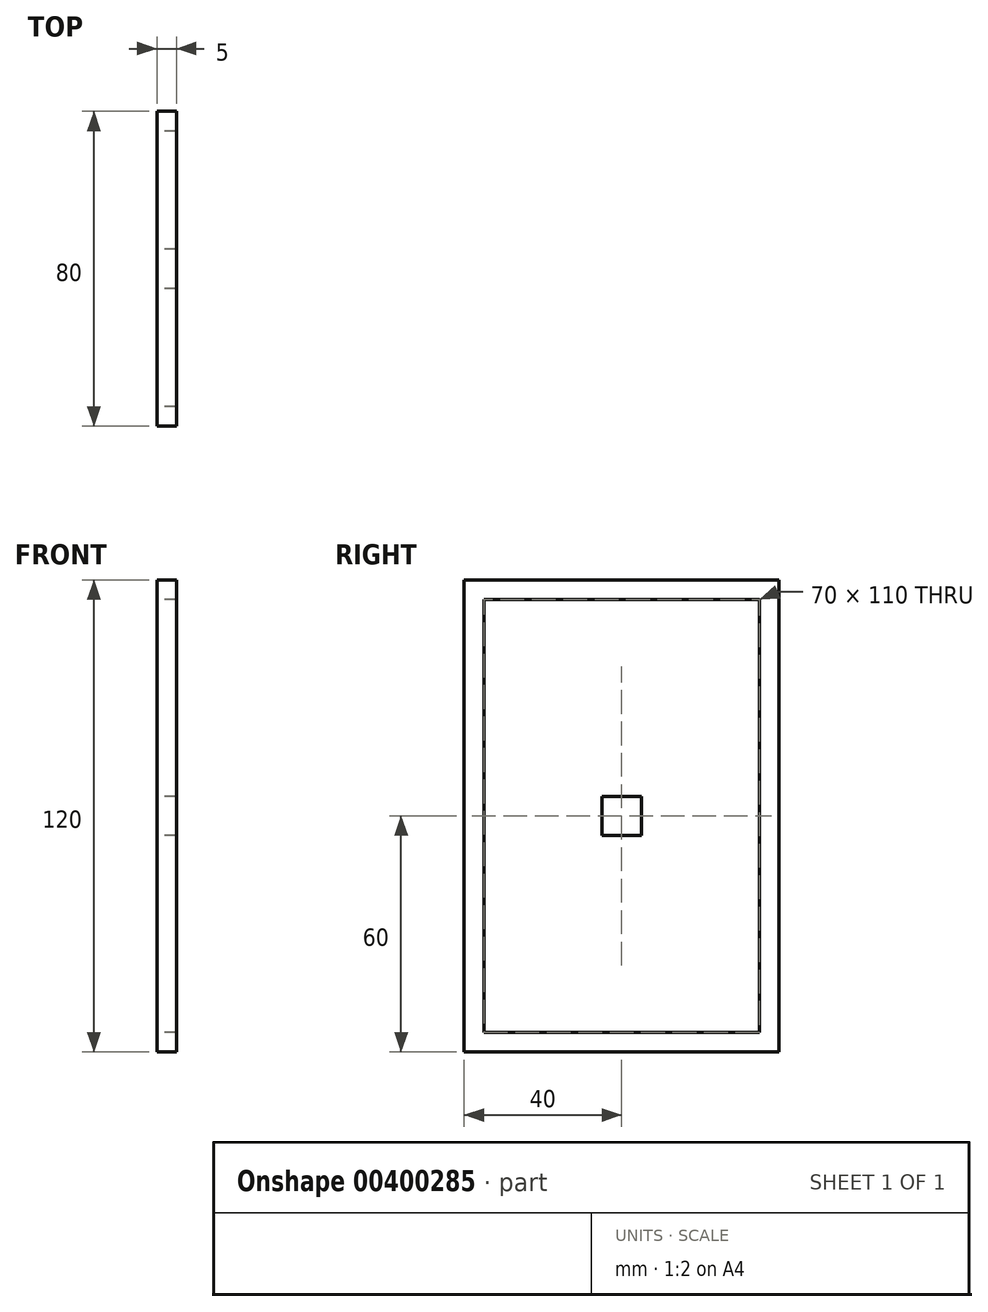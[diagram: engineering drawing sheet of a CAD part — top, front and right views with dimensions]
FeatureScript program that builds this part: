
annotation { "Feature Type Name" : "Feature", "Feature Type Description" : "" }
export const myFeature = defineFeature(function(context is Context, id is Id, definition is map)
    precondition{}
    {
        {
            var Q0;
            Q0=qCreatedBy(makeId("Right.planeOp"),FACE);
            var sketch = newSketch(context, id + "F0", { "sketchPlane" : qUnion([Q0])});
            skLineSegment(sketch, "E0.bottom", {"start": v(40, -60) * mm, "end": v(-40, -60) * mm});
            skLineSegment(sketch, "E0.top", {"start": v(40, 60) * mm, "end": v(-40, 60) * mm});
            skLineSegment(sketch, "E0.left", {"start": v(40, -60) * mm, "end": v(40, 60) * mm});
            skLineSegment(sketch, "E0.right", {"start": v(-40, -60) * mm, "end": v(-40, 60) * mm});
            skPoint(sketch, "E0.middle", {"position": v(0, 0) * mm});
            skLineSegment(sketch, "E1.bottom", {"start": v(35, -55) * mm, "end": v(-35, -55) * mm});
            skLineSegment(sketch, "E1.top", {"start": v(35, 55) * mm, "end": v(-35, 55) * mm});
            skLineSegment(sketch, "E1.left", {"start": v(35, -55) * mm, "end": v(35, 55) * mm});
            skLineSegment(sketch, "E1.right", {"start": v(-35, -55) * mm, "end": v(-35, 55) * mm});
            skLineSegment(sketch, "E2.bottom", {"start": v(35, -5) * mm, "end": v(-35, -5) * mm});
            skLineSegment(sketch, "E2.top", {"start": v(35, 5) * mm, "end": v(-35, 5) * mm});
            skLineSegment(sketch, "E2.left", {"start": v(35, -5) * mm, "end": v(35, 5) * mm});
            skLineSegment(sketch, "E2.right", {"start": v(-35, -5) * mm, "end": v(-35, 5) * mm});
            skLineSegment(sketch, "E3.bottom", {"start": v(5, -55) * mm, "end": v(-5, -55) * mm});
            skLineSegment(sketch, "E3.top", {"start": v(5, 55) * mm, "end": v(-5, 55) * mm});
            skLineSegment(sketch, "E3.left", {"start": v(5, -55) * mm, "end": v(5, 55) * mm});
            skLineSegment(sketch, "E3.right", {"start": v(-5, -55) * mm, "end": v(-5, 55) * mm});
            skSolve(sketch);
        }
        {
            var Q0;
            {var subQ0=sQuery(id+"F0.wireOp",EDGE,"E2.right");Q0=makeQuery(id+"F0.imprint","IMPRINT",FACE,{"disambiguationData":[TD([[makeQuery(id+"F0.imprint","IMPRINT",EDGE,{"derivedFrom":subQ0}),-1.0]])]});}
            var Q1;
            Q1=makeQuery(id+"F0.imprint","IMPRINT",FACE,{"disambiguationData":[TD([[makeQuery(id+"F0.imprint","IMPRINT",EDGE,{"derivedFrom":sQuery(id+"F0.wireOp",EDGE,"E0.bottom")}),-1.0]])]});
            var Q2;
            {var subQ5=sQuery(id+"F0.wireOp",EDGE,"E3.bottom");Q2=makeQuery(id+"F0.imprint","IMPRINT",FACE,{"disambiguationData":[TD([[makeQuery(id+"F0.imprint","IMPRINT",EDGE,{"derivedFrom":subQ5}),-1.0]])]});}
            var Q3;
            {var subQ0=sQuery(id+"F0.wireOp",EDGE,"E3.left");var subQ1=sQuery(id+"F0.wireOp",EDGE,"E2.bottom");var subQ2=makeQuery(id+"F0.imprint","INTERSECT",VERTEX,{"derivedFrom":[subQ1,subQ0]});Q3=makeQuery(id+"F0.imprint","IMPRINT",FACE,{"disambiguationData":[TD([[makeQuery(id+"F0.imprint","IMPRINT",EDGE,{"disambiguationData":[TD([[subQ2,-1.0]])],"derivedFrom":subQ1}),-1.0]])]});}
            var Q4;
            {var subQ0=sQuery(id+"F0.wireOp",EDGE,"E2.left");Q4=makeQuery(id+"F0.imprint","IMPRINT",FACE,{"disambiguationData":[TD([[makeQuery(id+"F0.imprint","IMPRINT",EDGE,{"derivedFrom":subQ0}),1.0]])]});}
            var Q5;
            {var subQ5=sQuery(id+"F0.wireOp",EDGE,"E3.top");Q5=makeQuery(id+"F0.imprint","IMPRINT",FACE,{"disambiguationData":[TD([[makeQuery(id+"F0.imprint","IMPRINT",EDGE,{"derivedFrom":subQ5}),1.0]])]});}
            extrude(context, id + "F1", {"entities" : qUnion([Q0, Q1, Q2, Q3, Q4, Q5]), "depth" : 5 * mm});
        }
    });
